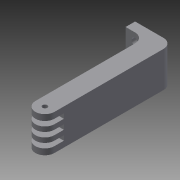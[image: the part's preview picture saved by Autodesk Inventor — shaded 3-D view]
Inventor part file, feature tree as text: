
AUTODESK INVENTOR PART (.ipt)
format: ipt  version: 2015 (Build 190159000, 159)  size: 158,208 bytes
history: native  units: mm
features: extrude x4, sketch x4, fillet x2
ambient origin geometry x8: Origin, YZ Plane, XZ Plane, XY Plane, X Axis, Y Axis, Z Axis, Center Point
bodies: Solid1 (feature_tree)
feature tree (10):
  extrude  "Extrusion1"  Depth=8.0mm
  extrude  "Extrusion2"  Depth=54.0mm
  extrude  "Extrusion3"  Depth=3.5mm
  fillet  "Fillet1"  Radius=8.75mm
  extrude  "Extrusion4"  Depth=4.0mm
  fillet  "Fillet2"  Radius=2.0mm
  sketch  "Sketch1"  dims[d0=50.0mm d3=8.0mm]
  sketch  "Sketch2"  dims[d4=15.0mm d5=0.0mm d7=54.0mm]
  sketch  "Sketch3"  dims[d12=3.5mm d13=3.5mm d16=8.75mm d17=0.0mm]
  sketch  "Sketch4"  dims[d18=8.0mm d19=1.0mm d20=2.0mm d21=2.0mm d22=2.0mm d23=2.0mm d24=2.0mm d25=10.0mm d26=10.25mm d27=0.0mm d28=16.0mm d29=3.5mm d30=3.5mm d31=3.0mm d32=3.0mm d33=4.0mm d34=2.0mm d35=21.0mm d36=0.0mm d37=4.0mm]
